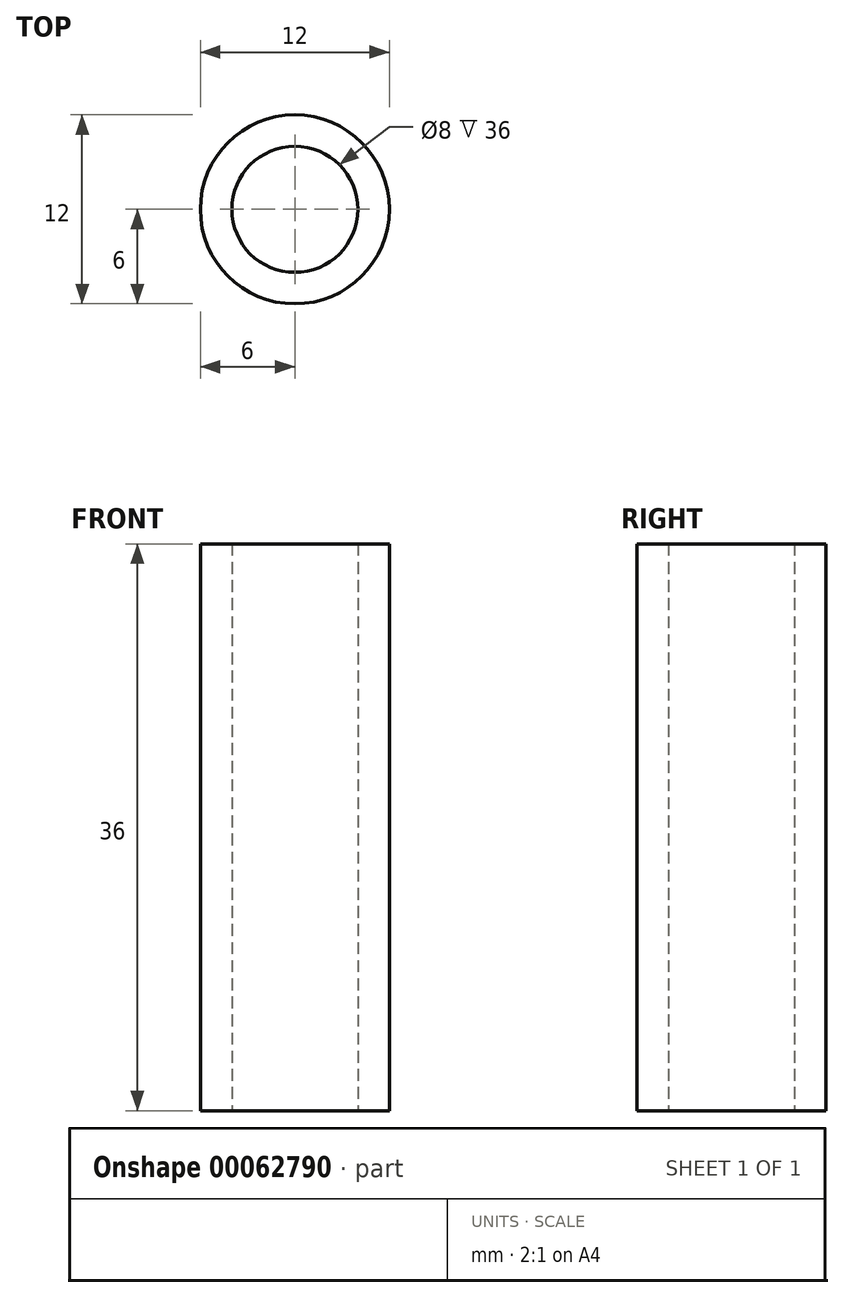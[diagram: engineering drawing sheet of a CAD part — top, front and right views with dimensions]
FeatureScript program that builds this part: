
annotation { "Feature Type Name" : "Feature", "Feature Type Description" : "" }
export const myFeature = defineFeature(function(context is Context, id is Id, definition is map)
    precondition{}
    {
        {
            var Q0;
            Q0=qCreatedBy(makeId("Top.planeOp"),FACE);
            var sketch = newSketch(context, id + "F0", { "sketchPlane" : qUnion([Q0])});
            skCircle(sketch, "E0", {"center": v(0, 0) * mm, "radius": 6 * mm});
            skCircle(sketch, "E1", {"center": v(0, 0) * mm, "radius": 4 * mm});
            skSolve(sketch);
        }
        {
            var Q0;
            Q0 = qSketchRegion(id + "F0", true);
            extrude(context, id + "F1", {"entities" : qUnion([Q0]), "depth" : 36 * mm});
        }
    });
